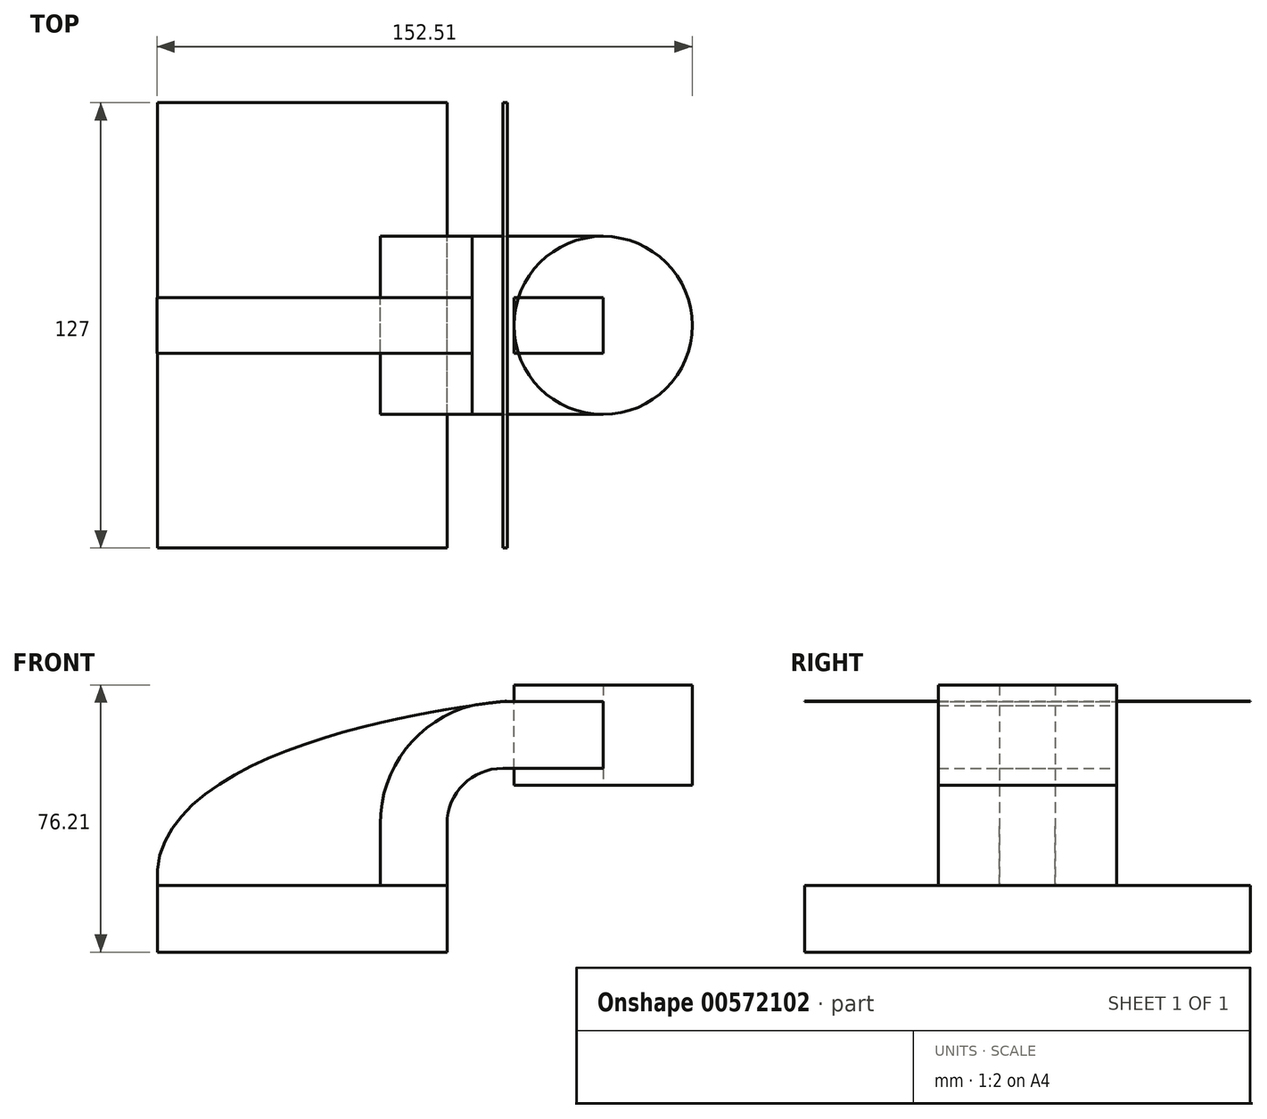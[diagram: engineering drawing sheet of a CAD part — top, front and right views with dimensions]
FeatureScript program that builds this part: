
annotation { "Feature Type Name" : "Feature", "Feature Type Description" : "" }
export const myFeature = defineFeature(function(context is Context, id is Id, definition is map)
    precondition{}
    {
        {
            var Q0;
            Q0=qCreatedBy(makeId("Front.planeOp"),FACE);
            var sketch = newSketch(context, id + "F0", { "sketchPlane" : qUnion([Q0])});
            skLineSegment(sketch, "E0.bottom", {"start": v(41.28, -9.52) * mm, "end": v(-41.28, -9.53) * mm});
            skLineSegment(sketch, "E0.top", {"start": v(41.27, 9.53) * mm, "end": v(-41.28, 9.53) * mm});
            skLineSegment(sketch, "E0.left", {"start": v(41.28, -9.52) * mm, "end": v(41.28, 9.53) * mm});
            skLineSegment(sketch, "E0.right", {"start": v(-41.28, -9.52) * mm, "end": v(-41.28, 9.53) * mm});
            skPoint(sketch, "E0.middle", {"position": v(0, 0) * mm});
            skLineSegment(sketch, "E1.bottom", {"start": v(111.12, 38.1) * mm, "end": v(60.32, 38.1) * mm});
            skLineSegment(sketch, "E1.top", {"start": v(111.12, 66.68) * mm, "end": v(60.32, 66.68) * mm});
            skLineSegment(sketch, "E1.left", {"start": v(111.12, 38.1) * mm, "end": v(111.12, 66.68) * mm});
            skLineSegment(sketch, "E1.right", {"start": v(60.32, 38.1) * mm, "end": v(60.32, 66.67) * mm});
            skLineSegment(sketch, "E2", {"start": v(41.27, 9.53) * mm, "end": v(41.27, 27) * mm});
            skArc(sketch, "E3", {"start": v(57.15, 42.88) * mm, "mid": v(45.92, 38.23) * mm, "end": v(41.27, 27) * mm});
            skLineSegment(sketch, "E4", {"start": v(57.15, 42.88) * mm, "end": v(85.72, 42.88) * mm});
            skPoint(sketch, "E5", {"position": v(85.72, 38.1) * mm});
            skLineSegment(sketch, "E6.0", {"start": v(22.23, 9.53) * mm, "end": v(22.23, 27) * mm});
            skArc(sketch, "E6.1", {"start": v(57.15, 61.93) * mm, "mid": v(32.45, 51.7) * mm, "end": v(22.23, 27) * mm});
            skLineSegment(sketch, "E6.2", {"start": v(57.15, 61.93) * mm, "end": v(85.72, 61.93) * mm});
            skLineSegment(sketch, "E7", {"start": v(85.72, 66.68) * mm, "end": v(85.72, 38.1) * mm});
            skFitSpline(sketch, "E8", {"points": [v(58.48, 61.93) * mm, v(57.15, 61.93) * mm, v(-41.28, 9.53) * mm], "startDerivative": vector(-8.8, 2.86) * mm, "endDerivative": vector(11.9, -134.85) * mm});
            skSolve(sketch);
        }
        {
            var Q0;
            {var subQ0=sQuery(id+"F0.wireOp",EDGE,"E8");var subQ1=sQuery(id+"F0.wireOp",EDGE,"E6.2");var subQ3=makeQuery(id+"F0.imprint","INTERSECT",VERTEX,{"derivedFrom":[subQ1,subQ0]});Q0=makeQuery(id+"F0.imprint","IMPRINT",FACE,{"disambiguationData":[TD([[makeQuery(id+"F0.imprint","IMPRINT",EDGE,{"disambiguationData":[TD([[subQ3,1.0]])],"derivedFrom":subQ1}),1.0]])]});}
            var Q1;
            Q1=makeQuery(id+"F0.imprint","IMPRINT",FACE,{"disambiguationData":[TD([[makeQuery(id+"F0.imprint","IMPRINT",EDGE,{"derivedFrom":sQuery(id+"F0.wireOp",EDGE,"E0.bottom")}),-1.0]])]});
            extrude(context, id + "F1", {"entities" : qUnion([Q0, Q1]), "endBound" : BoundingType.SYMMETRIC, "depth" : 127 * mm, "offsetDistance" : 25.4 * mm});
        }
        {
            var Q0;
            {var subQ1=sQuery(id+"F0.wireOp",EDGE,"E2");Q0=makeQuery(id+"F0.imprint","IMPRINT",FACE,{"disambiguationData":[TD([[makeQuery(id+"F0.imprint","IMPRINT",EDGE,{"derivedFrom":subQ1}),1.0]])]});}
            var Q1;
            {var subQ0=sQuery(id+"F0.wireOp",EDGE,"E4");var subQ1=sQuery(id+"F0.wireOp",EDGE,"E1.right");var subQ2=makeQuery(id+"F0.imprint","INTERSECT",VERTEX,{"derivedFrom":[subQ1,subQ0]});Q1=makeQuery(id+"F0.imprint","IMPRINT",FACE,{"disambiguationData":[TD([[makeQuery(id+"F0.imprint","IMPRINT",EDGE,{"disambiguationData":[TD([[subQ2,-1.0]])],"derivedFrom":subQ1}),-1.0]])]});}
            extrude(context, id + "F2", {"entities" : qUnion([Q0, Q1]), "endBound" : BoundingType.SYMMETRIC, "depth" : 50.8 * mm, "offsetDistance" : 25.4 * mm});
        }
        {
            var Q0;
            {var subQ0=sQuery(id+"F0.wireOp",EDGE,"E1.right");var subQ1=sQuery(id+"F0.wireOp",EDGE,"E1.top");var subQ2=makeQuery(id+"F0.imprint","INTERSECT",VERTEX,{"derivedFrom":[subQ1,subQ0]});Q0=makeQuery(id+"F0.imprint","IMPRINT",FACE,{"disambiguationData":[TD([[makeQuery(id+"F0.imprint","IMPRINT",EDGE,{"disambiguationData":[TD([[subQ2,1.0]])],"derivedFrom":subQ1}),1.0]])]});}
            var Q1;
            {var subQ0=sQuery(id+"F0.wireOp",EDGE,"E1.right");var subQ1=sQuery(id+"F0.wireOp",EDGE,"E1.bottom");var subQ2=makeQuery(id+"F0.imprint","INTERSECT",VERTEX,{"derivedFrom":[subQ1,subQ0]});Q1=makeQuery(id+"F0.imprint","IMPRINT",FACE,{"disambiguationData":[TD([[makeQuery(id+"F0.imprint","IMPRINT",EDGE,{"disambiguationData":[TD([[subQ2,1.0]])],"derivedFrom":subQ1}),-1.0]])]});}
            var Q2;
            {var subQ3=sQuery(id+"F0.wireOp",EDGE,"E6.0");Q2=makeQuery(id+"F0.imprint","IMPRINT",FACE,{"disambiguationData":[TD([[makeQuery(id+"F0.imprint","IMPRINT",EDGE,{"derivedFrom":subQ3}),1.0]])]});}
            extrude(context, id + "F3", {"entities" : qUnion([Q0, Q1, Q2]), "endBound" : BoundingType.SYMMETRIC, "depth" : 15.88 * mm, "offsetDistance" : 25.4 * mm});
        }
        {
            var Q0;
            {var subQ4=sQuery(id+"F0.wireOp",EDGE,"E1.left");Q0=makeQuery(id+"F0.imprint","IMPRINT",FACE,{"disambiguationData":[TD([[makeQuery(id+"F0.imprint","IMPRINT",EDGE,{"derivedFrom":subQ4}),1.0]])]});}
            var Q1;
            Q1=sQuery(id+"F0.wireOp",EDGE,"E7");
            revolve(context, id + "F4", {"entities" : qUnion([Q0]), "axis" : qUnion([Q1]), "revolveType" : RevolveType.FULL});
        }
    });
